# Revit family: Sanitary_Toilets_TOTO-USA-Inc_DuofitR-In-Wall-Tank-System-1-28-GPF-09
name_source: partatom
category: Plumbing Fixtures
revit_build: Autodesk Revit 2015 (Build: 20140606_1530(x64)
units: mm (PartAtom-declared; Revit-internal decimal feet)

## types (1)
- WT172M
    BIMobject category = Toilets
    BIMobject category code = sanitary-toilets
    BIMobject main category = Sanitary
    BIMobject main category code = sanitary
    Brand url = https://www.totousa.com
    Default Elevation = 4' - 0"
    Description = In-Wall Tank System with Dual-Max® Flushing System for the RP and SP wall-hung toilets.
    Edition number = 1
    IFC Classification = Flow Terminal
    Installation instructions = https://www.totousa.com
    Manufacturer = TOTO
    Manufacturer name = TOTO USA Inc
    Masterformat 2014 Code = 10 28 00
    Masterformat 2014 Description = Toilet, Bath, and Laundry Accessories
    Material Black = Plastic - TOTO - Black
    Material Blue = Metal - TOTO - Blue
    Material Steel = Metal - TOTO - Steel
    Material main = Ceramics
    Model = WT172M
    Nominal height = 0' - 0"
    Nominal width = 0' - 0"
    OmniClass Code = 23-31 19 00
    OmniClass Description = Toilets
    Product Guid = b0968435-5038-4b95-a74f-91a117bf7863
    Product SKU = toto-wt172m
    Product certification = https://www.totousa.com
    Product data url = https://bimobject.com
    Product family = Toilet and Bath Specialties
    Product group = Duofit??
    Product url = https://www.totousa.com
    QR code = http://bimobject.com
    Technical description = https://www.totousa.com
    UNSPSC Code = 30181505
    URL = www.totousa.com
    Uniclass 1.4 Code = L7216
    Uniclass 1.4 Description = Toilets
    Uniclass 2.0 Code = SS-35-65-90
    Uniclass 2.0 Description = Toilet Systems
    Uniclass 2015 Code = SL_35_80_89
    Uniclass 2015 Name = Toilets
    Uniformat II Code = D2030
    Uniformat II Description = Sanitary Waste
    Warranty = One year limited
    Water Supply Pressure(Min) = 55158.1 Pa

## geometry (parser evidence)
native form markers: Blend x4, Sweep x3
no freeform markers — native parametric forms only
